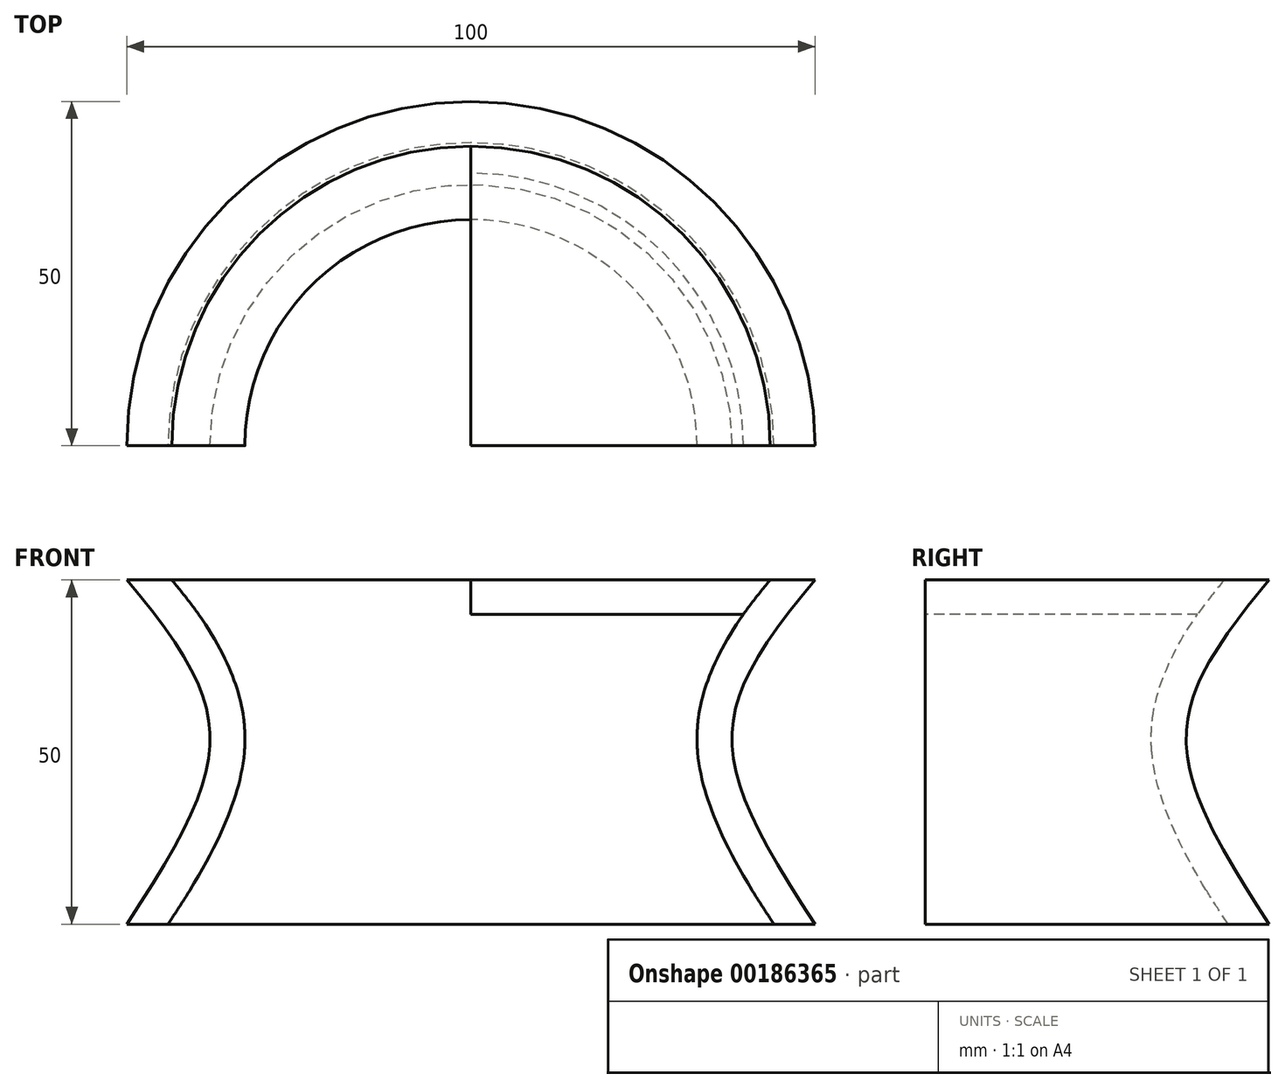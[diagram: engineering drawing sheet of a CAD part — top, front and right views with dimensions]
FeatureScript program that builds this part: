
annotation { "Feature Type Name" : "Feature", "Feature Type Description" : "" }
export const myFeature = defineFeature(function(context is Context, id is Id, definition is map)
    precondition{}
    {
        {
            var Q0;
            Q0=qCreatedBy(makeId("Front.planeOp"),FACE);
            var sketch = newSketch(context, id + "F0", { "sketchPlane" : qUnion([Q0])});
            skLineSegment(sketch, "E0", {"start": v(0, 50) * mm, "end": v(50, 50) * mm});
            skLineSegment(sketch, "E1", {"start": v(0, 0) * mm, "end": v(50, 0) * mm});
            skLineSegment(sketch, "E2", {"start": v(0, 50) * mm, "end": v(0, 0) * mm});
            skFitSpline(sketch, "E3", {"points": [v(50, 50) * mm, v(50, 0) * mm], "startDerivative": vector(-48.72, -58.02) * mm, "endDerivative": vector(47.84, -72.81) * mm});
            skLineSegment(sketch, "E4", {"start": v(0, 45) * mm, "end": v(39.75, 45) * mm});
            skLineSegment(sketch, "E5", {"start": v(0, 5) * mm, "end": v(40.92, 5) * mm});
            skLineSegment(sketch, "E6", {"start": v(33.12, 29.93) * mm, "end": v(0, 29.93) * mm});
            skLineSegment(sketch, "E7", {"start": v(33.01, 24.93) * mm, "end": v(0, 24.93) * mm});
            skFitSpline(sketch, "E8.0", {"points": [v(46.17, 53.22) * mm, v(44.1, 50.74) * mm, v(40.42, 46.15) * mm, v(36.96, 40.88) * mm, v(34.92, 36.67) * mm, v(33.78, 33.46) * mm, v(33.07, 30.17) * mm, v(32.85, 26.83) * mm, v(33.1, 23.46) * mm, v(33.81, 20.1) * mm, v(34.92, 16.7) * mm, v(36.9, 12.08) * mm, v(40.23, 5.96) * mm, v(43.8, 0.33) * mm, v(45.82, -2.75) * mm]});
            skSolve(sketch);
        }
        {
            var Q0;
            {var subQ4=sQuery(id+"F0.wireOp",EDGE,"E3");Q0=makeQuery(id+"F0.imprint","IMPRINT",FACE,{"disambiguationData":[TD([[makeQuery(id+"F0.imprint","IMPRINT",EDGE,{"derivedFrom":subQ4}),-1.0]])]});}
            var Q1;
            Q1=sQuery(id+"F0.wireOp",EDGE,"E2");
            revolve(context, id + "F1", {"entities" : qUnion([Q0]), "axis" : qUnion([Q1]), "revolveType" : RevolveType.ONE_DIRECTION, "oppositeDirection" : true, "angle" : 180 * degree});
        }
        {
            var Q0;
            {var subQ0=sQuery(id+"F0.wireOp",EDGE,"E2");var subQ1=sQuery(id+"F0.wireOp",EDGE,"E0");var subQ2=makeQuery(id+"F0.imprint","INTERSECT",VERTEX,{"derivedFrom":[subQ1,subQ0]});Q0=makeQuery(id+"F0.imprint","IMPRINT",FACE,{"disambiguationData":[TD([[makeQuery(id+"F0.imprint","IMPRINT",EDGE,{"disambiguationData":[TD([[subQ2,-1.0]])],"derivedFrom":subQ1}),-1.0]])]});}
            var Q1;
            Q1=makeQuery(id+"F1.opRevolve","SWEPT_BODY",BODY,{"disambiguationData":[OSD([sQuery(id+"F0.wireOp",EDGE,"E3"),sQuery(id+"F0.wireOp",EDGE,"fHZdtqhk-20Nc-RD7j-uQ2a-mzvSC5cLOukT")])]});
            extrude(context, id + "F2", {"entities" : qUnion([Q0]), "endBound" : BoundingType.UP_TO_BODY, "oppositeDirection" : true, "endBoundEntityBody" : qUnion([Q1]), "depth" : 25 * mm});
        }
    });
